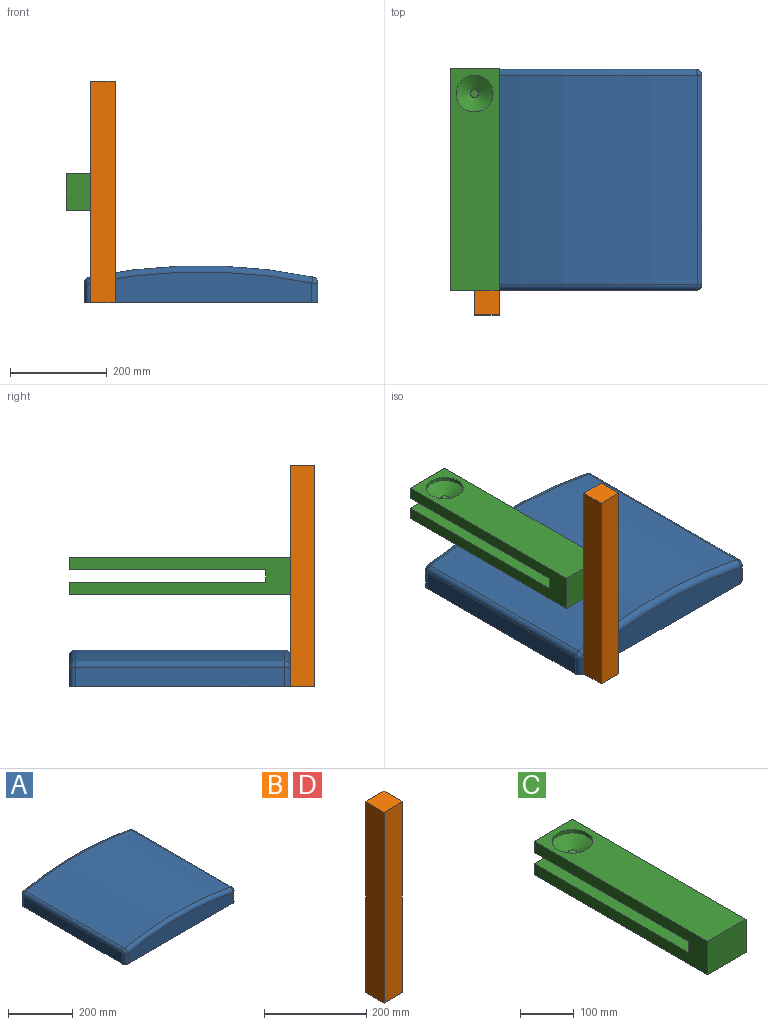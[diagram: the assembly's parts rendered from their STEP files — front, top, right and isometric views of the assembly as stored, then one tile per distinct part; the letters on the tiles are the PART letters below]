
ASSEMBLY  parts=4 mates=2
PART A: 18 faces, bbox 500.4x457.2x171.7 mm
  f0: cylinder r=1158.88mm len=462.27mm, axis (0,1,0), area 200954mm2, adj f9,f10,f14,f15
  f1: plane 457.2x63.5mm, normal (0,-1,0), area 25537mm2, adj f5,f6,f10,f11
  f2: plane 457.2x63.5mm, normal (0,1,0), area 25537mm2, adj f5,f8,f14,f17
  f3: plane 431.8x40.47mm, normal (1,0,0), area 17475.8mm2, adj f5,f6,f8,f9
  f4: plane 431.8x40.47mm, normal (-1,0,0), area 17475.8mm2, adj f5,f11,f15,f17
  f5: plane 482.6x457.2mm, normal (0,0,-1), area 220506.3mm2, adj f1,f2,f3,f4,f6,f8,f11,f17
  f6: cylinder r=12.7mm len=40.47mm, axis (0,0,-1), area 807.4mm2, adj f1,f3,f5,f7
  f7: sphere r=12.7mm, area 221mm2, adj f6,f9,f10
  f8: cylinder r=12.7mm len=40.47mm, axis (0,0,1), area 807.4mm2, adj f2,f3,f5,f12
  f9: cylinder r=12.7mm len=431.8mm, axis (0,1,0), area 7512.9mm2, adj f0,f3,f7,f12
  f10: torus R=1146.17mm, axis (0,-1,0), area 9247.1mm2, adj f0,f1,f7,f13
  f11: cylinder r=12.7mm len=40.47mm, axis (0,0,1), area 807.4mm2, adj f1,f4,f5,f13
  f12: sphere r=12.7mm, area 221mm2, adj f8,f9,f14
  f13: sphere r=12.7mm, area 221mm2, adj f10,f11,f15
  f14: torus R=1146.17mm, axis (0,-1,0), area 9247.1mm2, adj f0,f2,f12,f16
  f15: cylinder r=12.7mm len=431.8mm, axis (0,1,0), area 7512.9mm2, adj f0,f4,f13,f16
  f16: sphere r=12.7mm, area 221mm2, adj f14,f15,f17
  f17: cylinder r=12.7mm len=40.47mm, axis (0,0,-1), area 807.4mm2, adj f2,f4,f5,f16
PART B: 6 faces, bbox 50.8x50.8x457.2 mm
  f0: plane 457.2x50.8mm, normal (0,-1,0), area 23225.8mm2, adj f1,f3,f4,f5
  f1: plane 457.2x50.8mm, normal (1,0,0), area 23225.8mm2, adj f0,f2,f4,f5
  f2: plane 457.2x50.8mm, normal (0,1,0), area 23225.8mm2, adj f1,f3,f4,f5
  f3: plane 457.2x50.8mm, normal (-1,0,0), area 23225.8mm2, adj f0,f2,f4,f5
  f4: plane 50.8x50.8mm, normal (0,0,1), area 2580.6mm2, adj f0,f1,f2,f3
  f5: plane 50.8x50.8mm, normal (0,0,-1), area 2580.6mm2, adj f0,f1,f2,f3
PART C: 12 faces, bbox 101.6x457.2x76.2 mm
  f0: plane 101.6x25.4mm, normal (0,1,0), area 2580.6mm2, adj f1,f7,f8,f9
  f1: plane 457.2x101.6mm, normal (0,0,1), area 41891.2mm2, adj f0,f2,f8,f9,f11
  f2: plane 101.6x76.2mm, normal (0,-1,0), area 7741.9mm2, adj f1,f3,f8,f9
  f3: plane 457.2x101.6mm, normal (0,0,-1), area 46451.5mm2, adj f2,f4,f8,f9
  f4: plane 101.6x25.4mm, normal (0,1,0), area 2580.6mm2, adj f3,f5,f8,f9
  f5: plane 406.4x101.6mm, normal (0,0,1), area 41290.2mm2, adj f4,f6,f8,f9
  f6: plane 101.6x25.4mm, normal (0,1,0), area 2580.6mm2, adj f5,f7,f8,f9
  f7: plane 406.4x101.6mm, normal (0,0,-1), area 41062.8mm2, adj f0,f6,f8,f9,f10
  f8: plane 457.2x76.2mm, normal (1,0,0), area 24516.1mm2, adj f0,f1,f2,f3,f4,f5,f6,f7
  f9: plane 457.2x76.2mm, normal (-1,0,0), area 24516.1mm2, adj f0,f1,f2,f3,f4,f5,f6,f7
  f10: cone r=0mm half-angle=59deg, axis (0,0,1), area 5054.9mm2, adj f7,f11
  f11: cylinder r=38.1mm len=76.2mm, axis (0,0,1), area 1824.1mm2, adj f1,f10
PART D: same geometry as B
PLACE A t=(115.23,193.89,-217.19)mm
PLACE B t=(-87.97,-60.11,-13.99)mm fixed
PLACE C t=(-113.37,137.11,-26.69)mm
PLACE D t=(-87.97,-60.11,-13.99)mm fixed
MATE fastened D.f2 <-> A.f1  axis (0,1,0) through (-113.37,-34.71,-242.59)mm
MATE fastened C.f2 <-> D.f2  axis (0,-1,0) through (-62.57,-34.71,-13.99)mm
